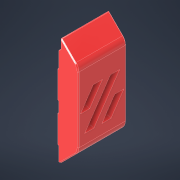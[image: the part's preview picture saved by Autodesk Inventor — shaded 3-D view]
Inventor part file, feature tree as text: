
AUTODESK INVENTOR PART (.ipt)
format: ipt  version: 2022.1 (Build 261234000, 234)  size: 584,704 bytes
history: native  units: mm
features: extrude x9, sketch x8, chamfer x7, projected_geometry x6, plane x3, reference x3, other x3, direct_edit x2, delete_face x2, fillet x2, move_body x2, hole x1
ambient origin geometry x8: Origin, YZ Plane, XZ Plane, XY Plane, X Axis, Y Axis, Z Axis, Center Point
bodies: Volumenkörper1 (feature_tree)
feature tree (48):
  extrude  "Extrusion1"  Depth=6.4mm
  plane  "Arbeitsebene1"
  extrude  "Extrusion2"  Depth=6.4mm
  chamfer  "Fase1"  Distance=6.4mm
  extrude  "Extrusion3"  Depth=10.0mm
  direct_edit  "Direktbearbeitung1"
  plane  "Arbeitsebene3"
  extrude  "Extrusion4"  Depth=10.0mm
  plane  "Arbeitsebene2"
  extrude  "Extrusion5"  Depth=10.0mm
  delete_face  "Fläche löschen1"
  extrude  "Extrusion7"  Depth=10.0mm TaperAngle=0.0deg
  extrude  "Extrusion8"  Depth=10.0mm
  chamfer  "Fase5"  Distance=7.9mm
  chamfer  "Fase6"  Distance=7.0mm Angle=45.0deg
  extrude  "Extrusion11"  TaperAngle=45.0deg  [1 undecoded]
  sketch  "Skizze13"  dims[d9=6.4mm d10=6.4mm d11=5.0mm d12=5.0mm d13=0.1mm d14=0.4mm d15=0.0mm d16=0.1mm d17=7.9mm d18=0.0mm d19=7.0mm d20=2.0mm d21=45.0deg d22=45.0deg d23=0.05mm d24=45.0deg d25=0.05mm d26=0.4mm d27=8.0mm d28=0.0mm d29=0.0mm d30=0.0mm d31=0.2mm d97=25.438174mm d99=3.8mm d102=3.304348mm d103=9.5mm d104=19.0mm d106=0.0mm d110=3.8mm d111=19.0mm d113=3.8mm d114=9.5mm d118=0.0mm d119=3.304348mm d124=15.705205mm d125=18.008696mm d126=25.215728mm d127=20.0mm d129=0.995652mm d130=1.0mm d131=0.0mm d146=20.0mm d147=10.0mm d148=12.607864mm d149=5.6mm d153=6.1mm d154=7.397555mm d155=2.198777mm d156=4.05mm d157=3.5mm d158=0.0mm d159=2.0mm d167=0.0mm d168=0.4mm d169=0.0mm d170=0.0mm d172=0.01mm d173=0.05mm d175=0.05mm d176=4.95mm d177=0.0mm d178=1.99mm d179=2.0mm d180=45.0deg d200=1.0mm d201=2.0mm d202=45.0deg d203=0.0mm d204=0.0mm d205=0.42mm d206=0.0mm d207=0.4mm d208=0.1mm d209=20.0mm d210=0.42mm d211=2.0mm d212=45.0deg d213=6.1mm d214=6.0mm d215=4.0mm d216=2.0mm d217=90.0deg d218=3.2mm d219=0.0mm d220=0.2mm d221=2.0mm d222=45.0deg d226=0.2mm d227=2.0mm d228=45.0deg d229=4.0mm d233=0.4mm d234=2.0mm d235=45.0deg d236=0.0mm d237=0.0mm d238=-0.5mm d171=0.872665mm]
  extrude  "Extrusion12"  Depth=10.0mm
  fillet  "Rundung7"  [1 undecoded]
  chamfer  "Fase7"  Distance=0.05mm
  hole  "Bohrung2"  [1 undecoded]
  chamfer  "Fase8"  Distance=8.0mm
  chamfer  "Fase10"  Distance=0.2mm
  fillet  "Rundung8"  Radius=25.438174mm
  chamfer  "Fase12"  Distance=3.8mm
  direct_edit  "Direktbearbeitung2"
  delete_face  "Fläche löschen2"
  sketch  "Skizze1"  dims[d0=3.25mm d1=6.4mm]
  reference  "Referenz1"
  sketch  "Skizze2"  dims[d2=6.4mm d3=6.4mm]
  reference  "Referenz2"
  sketch  "Skizze3"  dims[d4=6.4mm]
  projected_geometry  "Projizierte Kontur1"
  sketch  "Skizze6"  dims[d5=6.4mm]
  sketch  "Skizze8"  dims[d6=5.0mm]
  reference  "Referenz13"
  sketch  "Skizze9"  dims[d7=5.0mm]
  sketch  "Skizze12"  dims[d8=6.4mm]
  projected_geometry  "Projizierte Kontur3"
  projected_geometry  "Projizierte Kontur4"
  projected_geometry  "Projizierte Kontur5"
  projected_geometry  "Projizierte Kontur6"
  projected_geometry  "Projizierte Kontur7"
  other  "<userpath>\Desktop\Voron-2-2.4r1\Custom\Misumi GE5C\Gruppe.iam"
  other  "Gruppe.iam"
  other  "Z-Joint-Normal:1"
  move_body  "Verschieben1"
  move_body  "Verschieben2"
note: 3 required parameter values undecoded (feature->parameter linkage not recoverable at this tier; creation-order binding heuristic only, values carry confidence <= 0.55)
